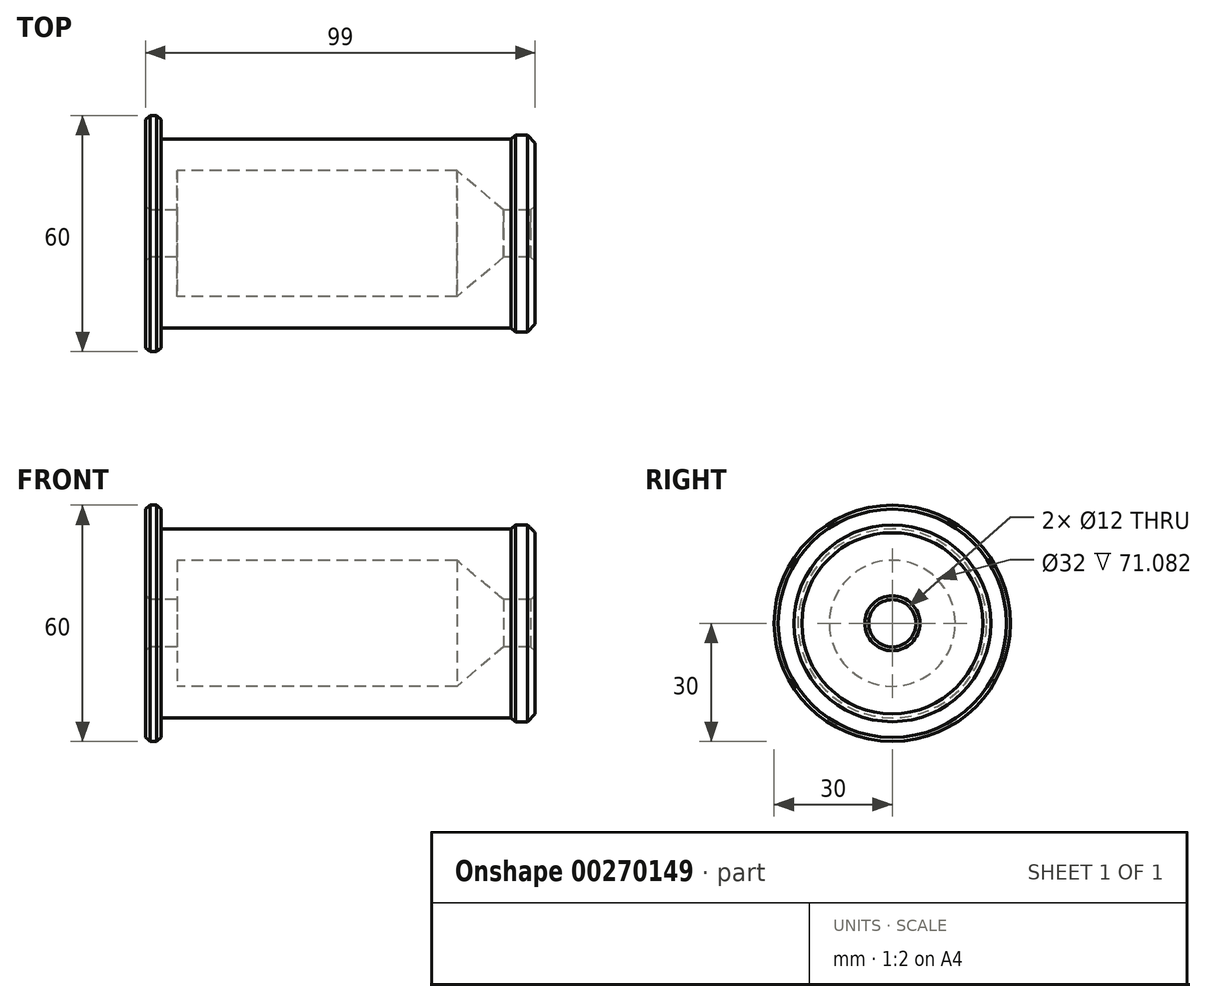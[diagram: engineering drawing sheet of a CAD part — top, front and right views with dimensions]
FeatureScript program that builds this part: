
annotation { "Feature Type Name" : "Feature", "Feature Type Description" : "" }
export const myFeature = defineFeature(function(context is Context, id is Id, definition is map)
    precondition{}
    {
        {
            var Q0;
            Q0=qCreatedBy(makeId("Front.planeOp"),FACE);
            var sketch = newSketch(context, id + "F0", { "sketchPlane" : qUnion([Q0])});
            skLineSegment(sketch, "E0", {"start": v(0, 0) * mm, "end": v(58.83, 0) * mm, "construction": true});
            skLineSegment(sketch, "E1", {"start": v(0, 6) * mm, "end": v(8, 6) * mm});
            skLineSegment(sketch, "E2", {"start": v(8, 6) * mm, "end": v(8, 16) * mm});
            skLineSegment(sketch, "E3", {"start": v(8, 16) * mm, "end": v(79.08, 16) * mm});
            skLineSegment(sketch, "E4", {"start": v(79.08, 16) * mm, "end": v(91, 6) * mm});
            skLineSegment(sketch, "E5", {"start": v(91, 6) * mm, "end": v(99, 6) * mm});
            skLineSegment(sketch, "E6", {"start": v(99, 6) * mm, "end": v(99, 25) * mm});
            skLineSegment(sketch, "E7", {"start": v(99, 25) * mm, "end": v(94, 25) * mm});
            skLineSegment(sketch, "E8", {"start": v(94, 25) * mm, "end": v(92.8, 24) * mm});
            skLineSegment(sketch, "E9", {"start": v(92.8, 24) * mm, "end": v(4, 24) * mm});
            skLineSegment(sketch, "E10", {"start": v(4, 24) * mm, "end": v(4, 30) * mm});
            skLineSegment(sketch, "E11", {"start": v(4, 30) * mm, "end": v(0, 30) * mm});
            skLineSegment(sketch, "E12", {"start": v(0, 30) * mm, "end": v(0, 6) * mm});
            skSolve(sketch);
        }
        {
            var Q0;
            Q0=makeQuery(id+"F0.imprint","IMPRINT",FACE,{"disambiguationData":[TD([[makeQuery(id+"F0.imprint","IMPRINT",EDGE,{"derivedFrom":sQuery(id+"F0.wireOp",EDGE,"E1")}),1.0]])]});
            var Q1;
            Q1=sQuery(id+"F0.wireOp",EDGE,"E0");
            revolve(context, id + "F1", {"entities" : qUnion([Q0]), "axis" : qUnion([Q1]), "revolveType" : RevolveType.FULL});
        }
        {
            var Q0;
            Q0=makeQuery(id+"F1.opRevolve","SWEPT_EDGE",EDGE,{"disambiguationData":[OSD([sQuery(id+"F0.wireOp",EDGE,"E1"),sQuery(id+"F0.wireOp",EDGE,"E12")])]});
            chamfer(context, id + "F2", {"entities" : qUnion([Q0]), "chamferType" : ChamferType.OFFSET_ANGLE, "width" : 1 * mm, "oppositeDirection" : true, "angle" : 50 * degree, "tangentPropagation" : true});
        }
        {
            var Q0;
            Q0=makeQuery(id+"F1.opRevolve","SWEPT_EDGE",EDGE,{"disambiguationData":[OSD([sQuery(id+"F0.wireOp",EDGE,"E5"),sQuery(id+"F0.wireOp",EDGE,"E6")])]});
            chamfer(context, id + "F3", {"entities" : qUnion([Q0]), "chamferType" : ChamferType.OFFSET_ANGLE, "width" : 1 * mm, "oppositeDirection" : false, "angle" : 50 * degree, "tangentPropagation" : true});
        }
        {
            var Q0;
            Q0=makeQuery(id+"F1.opRevolve","SWEPT_EDGE",EDGE,{"disambiguationData":[OSD([sQuery(id+"F0.wireOp",EDGE,"E6"),sQuery(id+"F0.wireOp",EDGE,"E7")])]});
            chamfer(context, id + "F4", {"entities" : qUnion([Q0]), "width" : 2 * mm, "tangentPropagation" : true});
        }
        {
            var Q0;
            Q0=makeQuery(id+"F1.opRevolve","SWEPT_EDGE",EDGE,{"disambiguationData":[OSD([sQuery(id+"F0.wireOp",EDGE,"E11"),sQuery(id+"F0.wireOp",EDGE,"E12")])]});
            chamfer(context, id + "F5", {"entities" : qUnion([Q0]), "chamferType" : ChamferType.OFFSET_ANGLE, "width" : 1 * mm, "oppositeDirection" : false, "angle" : 50 * degree, "tangentPropagation" : true});
        }
        {
            var Q0;
            Q0=makeQuery(id+"F1.opRevolve","SWEPT_EDGE",EDGE,{"disambiguationData":[OSD([sQuery(id+"F0.wireOp",EDGE,"E10"),sQuery(id+"F0.wireOp",EDGE,"E11")])]});
            chamfer(context, id + "F6", {"entities" : qUnion([Q0]), "chamferType" : ChamferType.OFFSET_ANGLE, "width" : 1 * mm, "oppositeDirection" : true, "angle" : 50 * degree, "tangentPropagation" : true});
        }
    });
